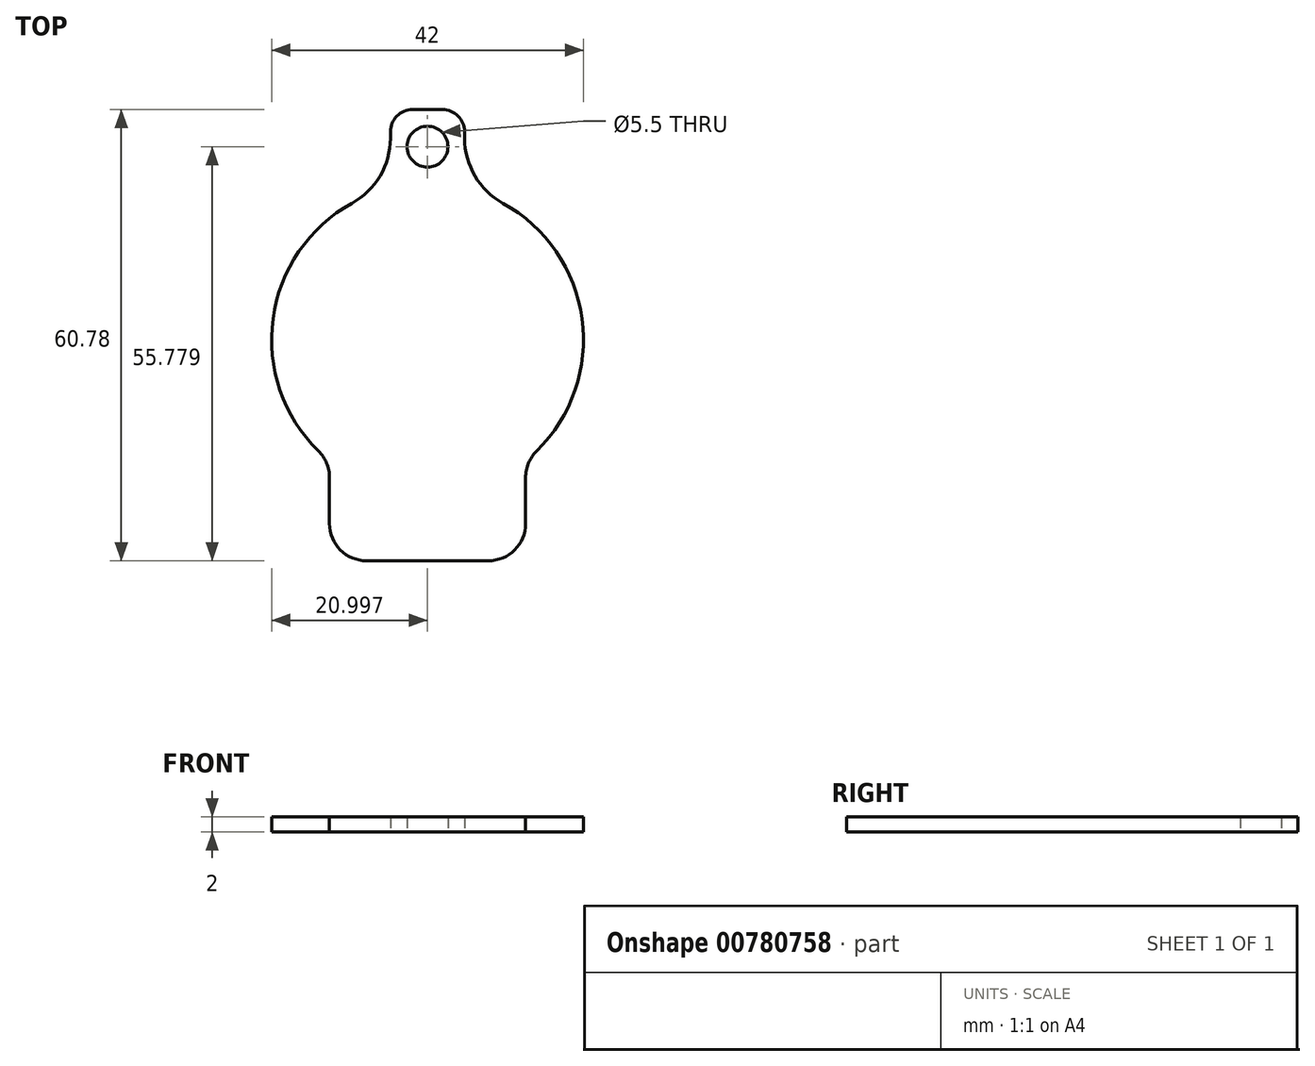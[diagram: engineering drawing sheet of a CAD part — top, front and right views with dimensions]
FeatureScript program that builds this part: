
annotation { "Feature Type Name" : "Feature", "Feature Type Description" : "" }
export const myFeature = defineFeature(function(context is Context, id is Id, definition is map)
    precondition{}
    {
        {
            var Q0;
            Q0=qCreatedBy(makeId("Top.planeOp"),FACE);
            var sketch = newSketch(context, id + "F0", { "sketchPlane" : qUnion([Q0])});
            skArc(sketch, "E0", {"start": v(14.48, -16.89) * mm, "mid": v(20.59, 0.94) * mm, "end": v(9.94, 16.49) * mm});
            skLineSegment(sketch, "E1.0", {"start": v(-0.22, -31.67) * mm, "end": v(7.98, -31.67) * mm});
            skPoint(sketch, "E2.orphan", {"position": v(2.83, -22.67) * mm});
            skLineSegment(sketch, "E3", {"start": v(-0.22, -1.9) * mm, "end": v(-0.22, -31.67) * mm, "construction": true});
            skLineSegment(sketch, "E4", {"start": v(12.98, -20.46) * mm, "end": v(12.98, -26.67) * mm});
            skPoint(sketch, "E5.visualSharp", {"position": v(12.98, -31.67) * mm});
            skArc(sketch, "E5.filletArc", {"start": v(7.98, -31.67) * mm, "mid": v(11.51, -30.2) * mm, "end": v(12.98, -26.67) * mm});
            skLineSegment(sketch, "E6.MirrorCS", {"start": v(-13.42, -20.46) * mm, "end": v(-13.42, -26.67) * mm});
            skArc(sketch, "E7.MirrorCS", {"start": v(-8.42, -31.67) * mm, "mid": v(-11.96, -30.2) * mm, "end": v(-13.42, -26.67) * mm});
            skLineSegment(sketch, "E8.MirrorCS", {"start": v(-0.22, -31.67) * mm, "end": v(-8.42, -31.67) * mm});
            skPoint(sketch, "E9.visualSharp", {"position": v(12.98, -18.22) * mm});
            skArc(sketch, "E9.filletArc", {"start": v(14.48, -16.89) * mm, "mid": v(13.37, -18.52) * mm, "end": v(12.98, -20.46) * mm});
            skPoint(sketch, "E10.visualSharp", {"position": v(-13.42, -18.22) * mm});
            skArc(sketch, "E10.filletArc", {"start": v(-13.42, -20.46) * mm, "mid": v(-13.81, -18.52) * mm, "end": v(-14.92, -16.89) * mm});
            skLineSegment(sketch, "E11", {"start": v(-0.22, -1.9) * mm, "end": v(-0.22, 34.97) * mm, "construction": true});
            skLineSegment(sketch, "E12.0", {"start": v(-0.22, 29.1) * mm, "end": v(-2.22, 29.1) * mm});
            skLineSegment(sketch, "E13.0", {"start": v(-5.22, 25.24) * mm, "end": v(-5.22, 26.1) * mm});
            skArc(sketch, "E14.trimOffspring", {"start": v(-10.38, 16.49) * mm, "mid": v(-21.03, 0.94) * mm, "end": v(-14.92, -16.89) * mm});
            skPoint(sketch, "E15.visualSharp", {"position": v(-5.22, 18.5) * mm});
            skArc(sketch, "E15.filletArc", {"start": v(-10.38, 16.49) * mm, "mid": v(-6.6, 20.16) * mm, "end": v(-5.22, 25.24) * mm});
            skPoint(sketch, "E16.visualSharp", {"position": v(-5.22, 29.1) * mm});
            skArc(sketch, "E16.filletArc", {"start": v(-2.22, 29.1) * mm, "mid": v(-4.34, 28.23) * mm, "end": v(-5.22, 26.1) * mm});
            skLineSegment(sketch, "E17.MirrorCS", {"start": v(-0.22, 29.1) * mm, "end": v(1.78, 29.1) * mm});
            skArc(sketch, "E18.MirrorCS", {"start": v(1.78, 29.1) * mm, "mid": v(3.9, 28.23) * mm, "end": v(4.78, 26.1) * mm});
            skLineSegment(sketch, "E19.MirrorCS", {"start": v(4.78, 25.24) * mm, "end": v(4.78, 26.1) * mm});
            skArc(sketch, "E20.MirrorCS", {"start": v(9.94, 16.49) * mm, "mid": v(6.16, 20.16) * mm, "end": v(4.78, 25.24) * mm});
            skPoint(sketch, "E21.orphan", {"position": v(-0.22, 19.1) * mm});
            skCircle(sketch, "E22", {"center": v(-0.22, 24.1) * mm, "radius": 2.75 * mm});
            skSolve(sketch);
        }
        {
            var Q0;
            Q0=makeQuery(id+"F0.imprint","IMPRINT",FACE,{"disambiguationData":[TD([[makeQuery(id+"F0.imprint","IMPRINT",EDGE,{"derivedFrom":sQuery(id+"F0.wireOp",EDGE,"E0")}),1.0]])]});
            extrude(context, id + "F1", {"entities" : qUnion([Q0]), "depth" : 2 * mm, "offsetDistance" : 25 * mm});
        }
    });
